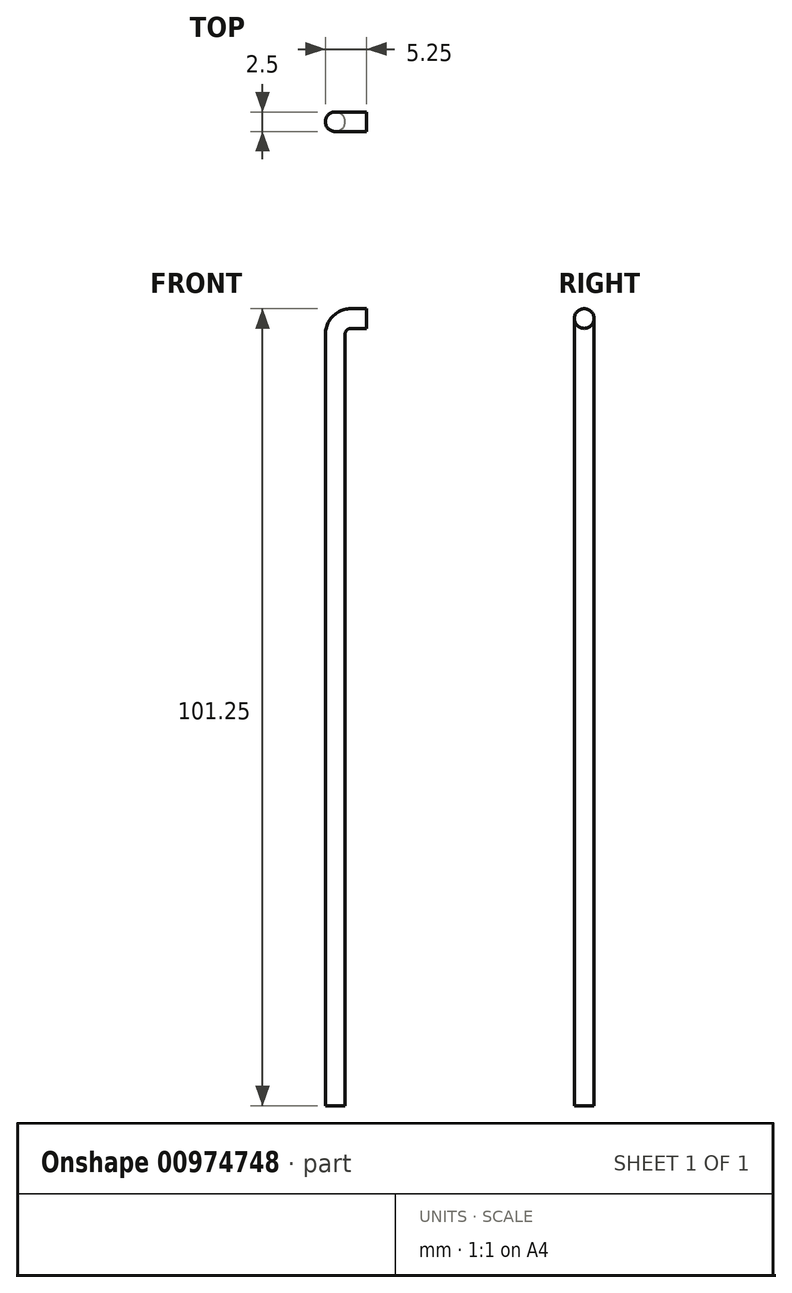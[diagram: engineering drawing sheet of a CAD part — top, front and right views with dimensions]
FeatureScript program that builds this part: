
annotation { "Feature Type Name" : "Feature", "Feature Type Description" : "" }
export const myFeature = defineFeature(function(context is Context, id is Id, definition is map)
    precondition{}
    {
        {
            var Q0;
            Q0=qCreatedBy(makeId("Top.planeOp"),FACE);
            var sketch = newSketch(context, id + "F0", { "sketchPlane" : qUnion([Q0])});
            skCircle(sketch, "E0", {"center": v(0, 0) * mm, "radius": 1.25 * mm});
            skSolve(sketch);
        }
        {
            var Q0;
            Q0=qCreatedBy(makeId("Front.planeOp"),FACE);
            var sketch = newSketch(context, id + "F1", { "sketchPlane" : qUnion([Q0])});
            skLineSegment(sketch, "E1", {"start": v(0, 0) * mm, "end": v(0, 98) * mm});
            skLineSegment(sketch, "E2", {"start": v(2, 100) * mm, "end": v(4, 100) * mm});
            skPoint(sketch, "E3.visualSharp", {"position": v(0, 100) * mm});
            skArc(sketch, "E3.filletArc", {"start": v(2, 100) * mm, "mid": v(0.59, 99.41) * mm, "end": v(0, 98) * mm});
            skSolve(sketch);
        }
        {
            var Q0;
            Q0 = qSketchRegion(id + "F0", true);
            var Q1;
            Q1 = qConstructionFilter(qBodyType(qCreatedBy(id + "F1" ,EDGE), BodyType.WIRE), ConstructionObject.NO);
            sweep(context, id + "F2", {"profiles" : qUnion([Q0]), "path" : qUnion([Q1])});
        }
    });
